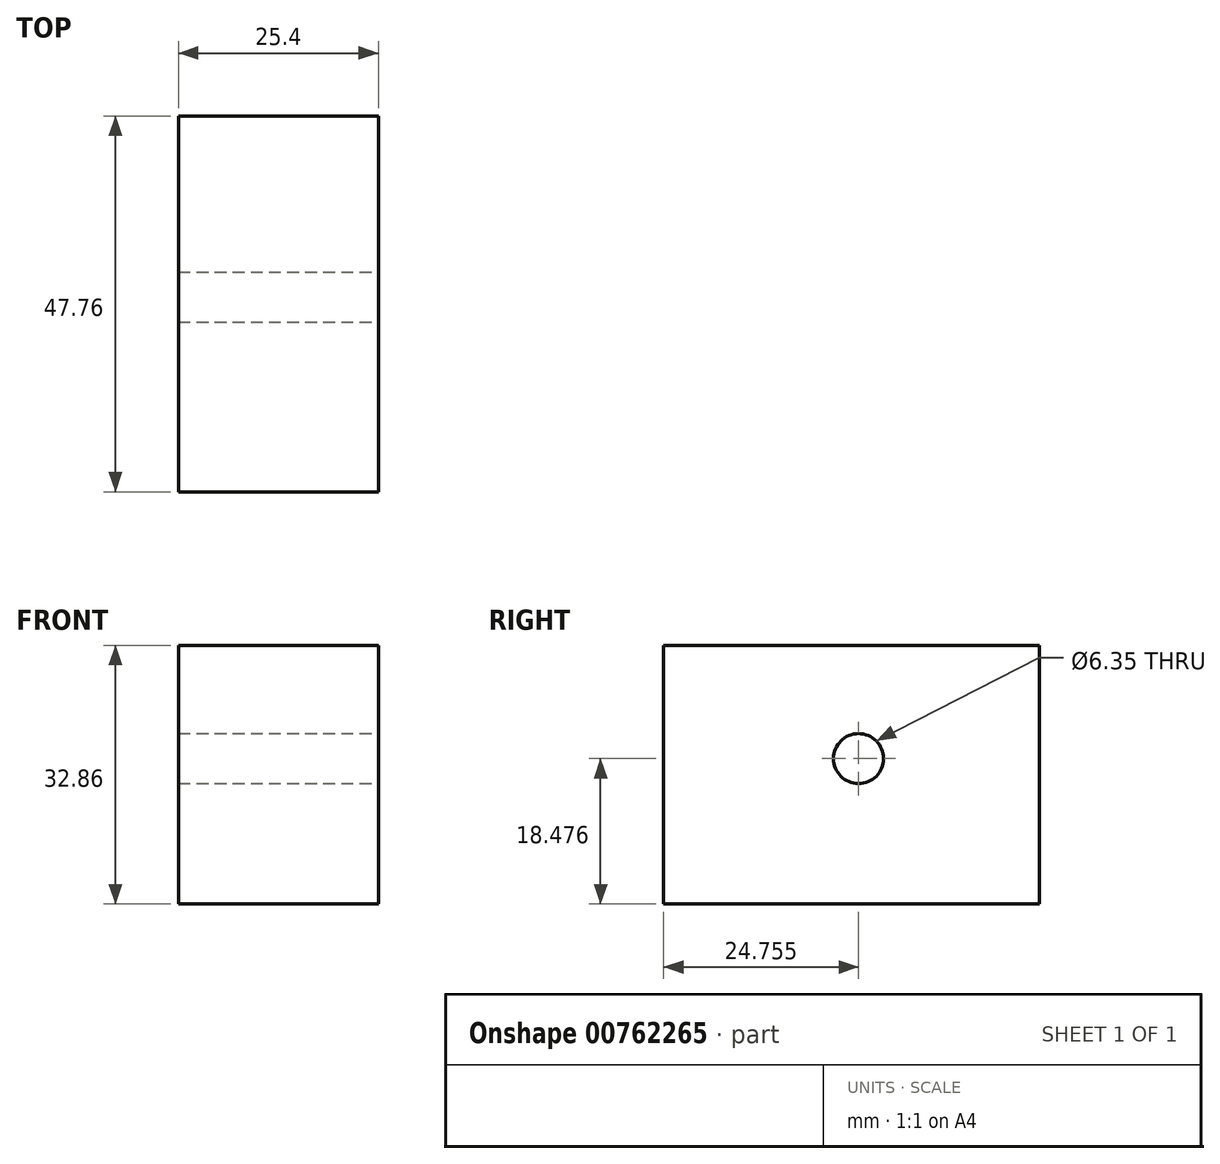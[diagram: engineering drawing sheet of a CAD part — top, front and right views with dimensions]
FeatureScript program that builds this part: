
annotation { "Feature Type Name" : "Feature", "Feature Type Description" : "" }
export const myFeature = defineFeature(function(context is Context, id is Id, definition is map)
    precondition{}
    {
        {
            var Q0;
            Q0=qCreatedBy(makeId("Right.planeOp"),FACE);
            var sketch = newSketch(context, id + "F0", { "sketchPlane" : qUnion([Q0])});
            skLineSegment(sketch, "E0.bottom", {"start": v(0, 0) * mm, "end": v(47.76, 0) * mm});
            skLineSegment(sketch, "E0.top", {"start": v(0, 32.86) * mm, "end": v(47.76, 32.86) * mm});
            skLineSegment(sketch, "E0.left", {"start": v(0, 0) * mm, "end": v(0, 32.86) * mm});
            skLineSegment(sketch, "E0.right", {"start": v(47.76, 0) * mm, "end": v(47.76, 32.86) * mm});
            skSolve(sketch);
        }
        {
            var Q0;
            Q0 = qSketchRegion(id + "F0", true);
            extrude(context, id + "F1", {"entities" : qUnion([Q0]), "depth" : 25.4 * mm, "offsetDistance" : 25.4 * mm});
        }
        {
            var Q0;
            Q0=makeQuery(id+"F1.opExtrude","CAP_FACE",FACE,{"disambiguationData":[OSD([sQuery(id+"F0.wireOp",EDGE,"E0.bottom"),sQuery(id+"F0.wireOp",EDGE,"E0.top"),sQuery(id+"F0.wireOp",EDGE,"E0.left"),sQuery(id+"F0.wireOp",EDGE,"E0.right")])],"isStart":false});
            var sketch = newSketch(context, id + "F2", { "sketchPlane" : qUnion([Q0])});
            skPoint(sketch, "E1", {"position": v(24.76, 18.48) * mm});
            skSolve(sketch);
        }
        {
            var Q0;
            Q0=sQuery(id+"F2.wireOp",VERTEX,"E1");
            var Q1;
            Q1=makeQuery(id+"F1.opExtrude","SWEPT_BODY",BODY,{"disambiguationData":[OSD([sQuery(id+"F0.wireOp",EDGE,"E0.bottom"),sQuery(id+"F0.wireOp",EDGE,"E0.top"),sQuery(id+"F0.wireOp",EDGE,"E0.left"),sQuery(id+"F0.wireOp",EDGE,"E0.right")])]});
            hole(context, id + "F3", {"style" : HoleStyle.SIMPLE, "endStyle" : HoleEndStyle.THROUGH, "holeDiameter" : 6.35 * mm, "majorDiameter" : 6.35 * mm, "isTappedThrough" : true, "tappedDepth" : 12.7 * mm, "tapClearance" : 3, "locations" : qUnion([Q0]), "scope" : qUnion([Q1])});
        }
    });
